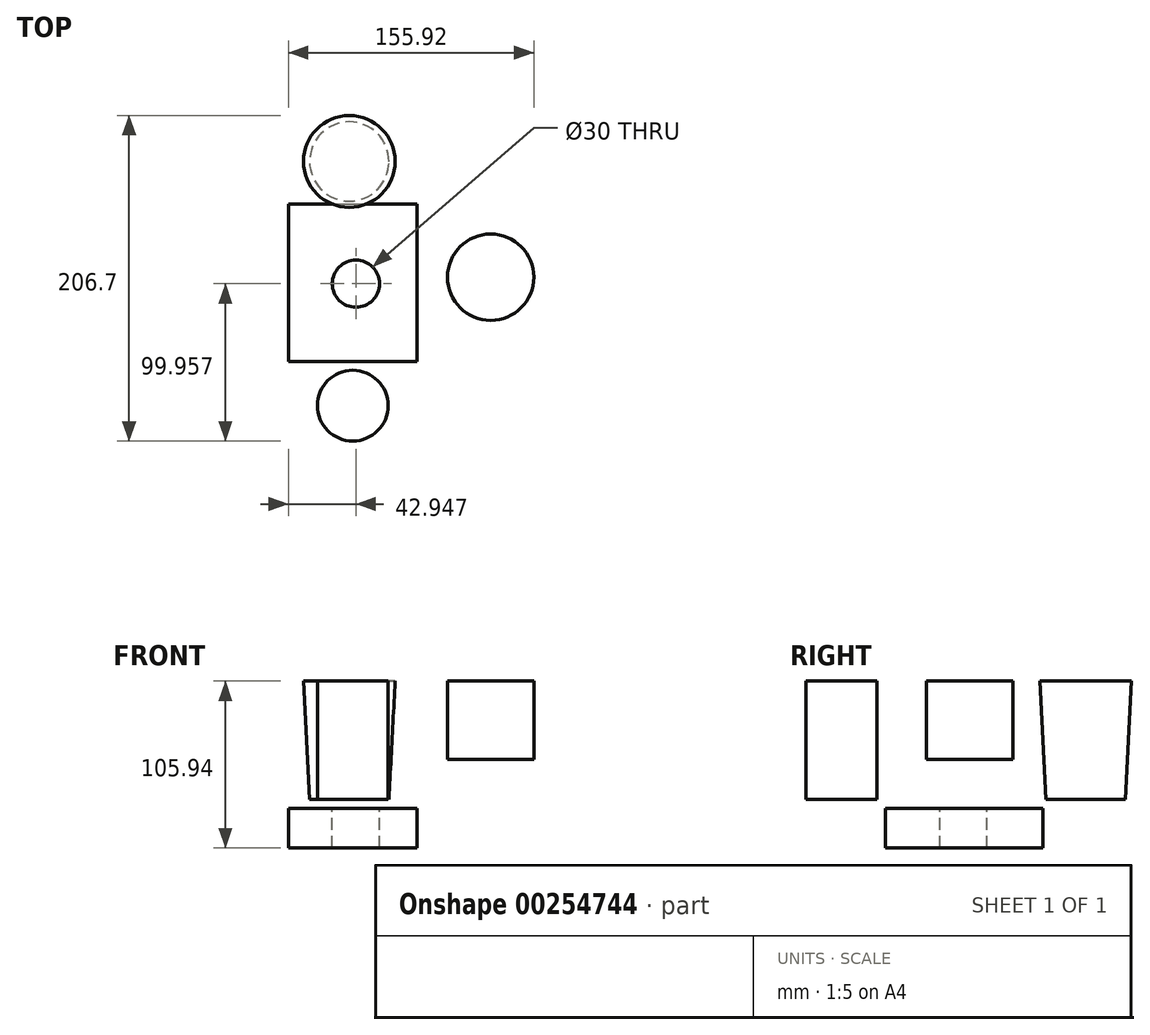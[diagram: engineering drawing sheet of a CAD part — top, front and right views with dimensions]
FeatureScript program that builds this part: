
annotation { "Feature Type Name" : "Feature", "Feature Type Description" : "" }
export const myFeature = defineFeature(function(context is Context, id is Id, definition is map)
    precondition{}
    {
        {
            var Q0;
            Q0=qCreatedBy(makeId("Front.planeOp"),FACE);
            var sketch = newSketch(context, id + "F0", { "sketchPlane" : qUnion([Q0])});
            skLineSegment(sketch, "E0.bottom", {"start": v(-24.75, -30.94) * mm, "end": v(56.87, -30.94) * mm});
            skLineSegment(sketch, "E0.top", {"start": v(-24.75, -5.9) * mm, "end": v(56.87, -5.9) * mm});
            skLineSegment(sketch, "E0.left", {"start": v(-24.75, -30.94) * mm, "end": v(-24.75, -5.9) * mm});
            skLineSegment(sketch, "E0.right", {"start": v(56.87, -30.94) * mm, "end": v(56.87, -5.9) * mm});
            skSolve(sketch);
        }
        {
            var Q0;
            Q0=makeQuery(id+"F0.imprint","IMPRINT",FACE,{"disambiguationData":[TD([[makeQuery(id+"F0.imprint","IMPRINT",EDGE,{"derivedFrom":sQuery(id+"F0.wireOp",EDGE,"E0.bottom")}),1.0]])]});
            extrude(context, id + "F1", {"entities" : qUnion([Q0]), "depth" : 100 * mm});
        }
        {
            var Q0;
            Q0=qCreatedBy(makeId("Top.planeOp"),FACE);
            var sketch = newSketch(context, id + "F2", { "sketchPlane" : qUnion([Q0])});
            skCircle(sketch, "E1", {"center": v(13.97, 27.03) * mm, "radius": 25.2 * mm});
            skSolve(sketch);
        }
        {
            var Q0;
            Q0=makeQuery(id+"F2.imprint","IMPRINT",FACE,{"disambiguationData":[TD([[makeQuery(id+"F2.imprint","IMPRINT",EDGE,{"derivedFrom":sQuery(id+"F2.wireOp",EDGE,"E1")}),1.0]])]});
            extrude(context, id + "F3", {"entities" : qUnion([Q0]), "depth" : 75 * mm, "hasDraft" : true, "draftAngle" : 3 * degree});
        }
        {
            var Q0;
            Q0=qCreatedBy(makeId("Top.planeOp"),FACE);
            var sketch = newSketch(context, id + "F4", { "sketchPlane" : qUnion([Q0])});
            skCircle(sketch, "E2", {"center": v(16.19, -128.05) * mm, "radius": 22.48 * mm});
            skSolve(sketch);
        }
        {
            var Q0;
            Q0=makeQuery(id+"F4.imprint","IMPRINT",FACE,{"disambiguationData":[TD([[makeQuery(id+"F4.imprint","IMPRINT",EDGE,{"derivedFrom":sQuery(id+"F4.wireOp",EDGE,"E2")}),1.0]])]});
            var sketch = newSketch(context, id + "F5", { "sketchPlane" : qUnion([Q0])});
            skSolve(sketch);
        }
        {
            var Q0;
            Q0 = qSketchRegion(id + "F5", true);
            var Q1;
            Q1=makeQuery(id+"F4.imprint","IMPRINT",FACE,{"disambiguationData":[TD([[makeQuery(id+"F4.imprint","IMPRINT",EDGE,{"derivedFrom":sQuery(id+"F4.wireOp",EDGE,"E2")}),1.0]])]});
            extrude(context, id + "F6", {"entities" : qUnion([Q0, Q1]), "depth" : 75 * mm});
        }
        {
            var Q0;
            Q0=qCreatedBy(makeId("Top.planeOp"),FACE);
            var sketch = newSketch(context, id + "F7", { "sketchPlane" : qUnion([Q0])});
            skCircle(sketch, "E3", {"center": v(103.75, -46.48) * mm, "radius": 27.43 * mm});
            skSolve(sketch);
        }
        {
            var Q0;
            Q0=makeQuery(id+"F7.imprint","IMPRINT",FACE,{"disambiguationData":[TD([[makeQuery(id+"F7.imprint","IMPRINT",EDGE,{"derivedFrom":sQuery(id+"F7.wireOp",EDGE,"E3")}),1.0]])]});
            extrude(context, id + "F8", {"entities" : qUnion([Q0]), "depth" : 75 * mm, "hasSecondDirection" : true, "secondDirectionOppositeDirection" : false, "secondDirectionDepth" : 25.4 * mm});
        }
        {
            var Q0;
            Q0=makeQuery(id+"F1.opExtrude","SWEPT_FACE",FACE,{"disambiguationData":[OSD([sQuery(id+"F0.wireOp",EDGE,"E0.top")])]});
            var sketch = newSketch(context, id + "F9", { "sketchPlane" : qUnion([Q0])});
            skPoint(sketch, "E4", {"position": v(18.2, -50.57) * mm});
            skSolve(sketch);
        }
        {
            var Q0;
            Q0=sQuery(id+"F9.wireOp",VERTEX,"E4");
            var Q1;
            Q1=makeQuery(id+"F1.opExtrude","SWEPT_BODY",BODY,{"disambiguationData":[OSD([sQuery(id+"F0.wireOp",EDGE,"E0.bottom"),sQuery(id+"F0.wireOp",EDGE,"E0.top"),sQuery(id+"F0.wireOp",EDGE,"E0.left"),sQuery(id+"F0.wireOp",EDGE,"E0.right")])]});
            hole(context, id + "F10", {"style" : HoleStyle.SIMPLE, "endStyle" : HoleEndStyle.THROUGH, "holeDiameter" : 30 * mm, "tappedDepth" : 12 * mm, "tapClearance" : 3, "locations" : qUnion([Q0]), "scope" : qUnion([Q1])});
        }
    });
